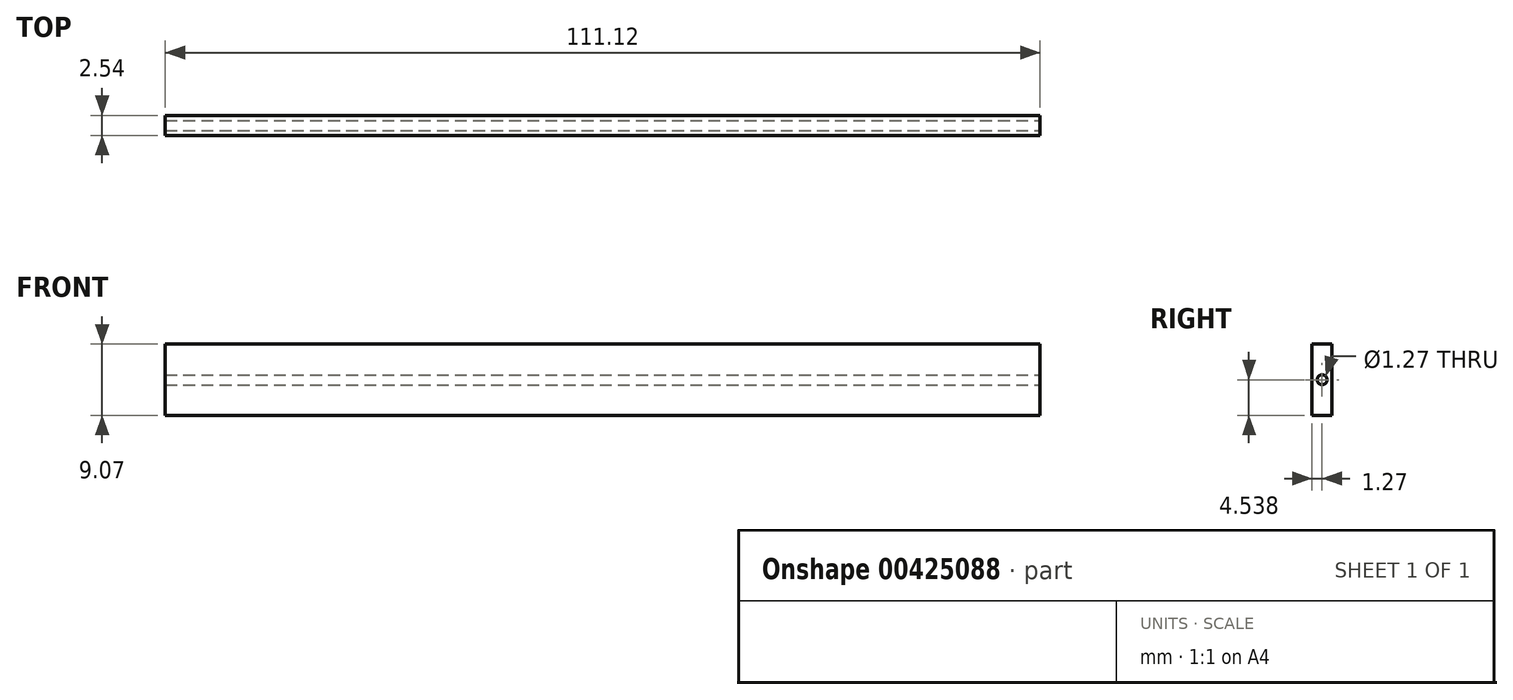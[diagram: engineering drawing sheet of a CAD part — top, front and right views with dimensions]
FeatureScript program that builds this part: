
annotation { "Feature Type Name" : "Feature", "Feature Type Description" : "" }
export const myFeature = defineFeature(function(context is Context, id is Id, definition is map)
    precondition{}
    {
        {
            var Q0;
            Q0=qCreatedBy(makeId("Front.planeOp"),FACE);
            var sketch = newSketch(context, id + "F0", { "sketchPlane" : qUnion([Q0])});
            skLineSegment(sketch, "E0.bottom", {"start": v(-27.34, -17.66) * mm, "end": v(83.78, -17.66) * mm});
            skLineSegment(sketch, "E0.top", {"start": v(-27.34, -26.73) * mm, "end": v(83.78, -26.73) * mm});
            skLineSegment(sketch, "E0.left", {"start": v(-27.34, -17.66) * mm, "end": v(-27.34, -26.73) * mm});
            skLineSegment(sketch, "E0.right", {"start": v(83.78, -17.66) * mm, "end": v(83.78, -26.73) * mm});
            skSolve(sketch);
        }
        {
            var Q0;
            Q0 = qSketchRegion(id + "F0", true);
            extrude(context, id + "F1", {"entities" : qUnion([Q0]), "oppositeDirection" : true, "depth" : 2.54 * mm});
        }
        {
            var Q0;
            Q0=makeQuery(id+"F1.opExtrude","SWEPT_FACE",FACE,{"disambiguationData":[OSD([sQuery(id+"F0.wireOp",EDGE,"E0.right")])]});
            var sketch = newSketch(context, id + "F2", { "sketchPlane" : qUnion([Q0])});
            skCircle(sketch, "E1", {"center": v(1.27, -22.2) * mm, "radius": 0.63 * mm});
            skPoint(sketch, "E1.centerSnap0", {"position": v(1.27, -17.66) * mm});
            skPoint(sketch, "E1.centerSnap1", {"position": v(2.54, -22.2) * mm});
            skSolve(sketch);
        }
        {
            var Q0;
            Q0 = qSketchRegion(id + "F2", true);
            extrude(context, id + "F3", {"entities" : qUnion([Q0]), "operationType" : NewBodyOperationType.REMOVE, "oppositeDirection" : true, "depth" : 131.83 * mm});
        }
    });
